# Revit family: 30. Секция фильтрования, вод. наг. и фреон. охл. ANR T4
name_source: partatom
category: Оборудование
revit_build: Autodesk Revit 2016 (Build: 20161004_0715(x64)
units: mm (PartAtom-declared; Revit-internal decimal feet)

## family parameters
Всегда вертикально = Да
На основе рабочей плоскости = Нет
Общий = Нет
При загрузке вырезать с полостями = Нет
Размер круглого соединителя = Использовать диаметр
Тип детали = Нормальный
Точка расчета площади = Нет

## types (10) — shared parameters
h = 130 мм
Д = 1625 мм
Д1 = 1605 мм
Д2 = 535 мм
Д3 = 268 мм
Е = 85 мм
Единица измерения = шт.
Завод изготовитель = KORF
Ключевая пометка = Вентиляция
Материал = Сталь серая
Наименование и тех.хар-ка = Секция фильтрования EU4, водяного нагрева вместе с фреоновым охлаждением
Раздел = ОВ
Размер В = 85 мм
Синий = Синий
высота ножек = 120 мм

## per-type parameters (varying)
| type | d | А | А1 | Б | Б1 | Вн | Высота | Г | Гн | Ж | З | И | Середина | Ширина |
| ANR 6 T4 | 32 мм | 1100 мм | 1080 мм | 1100 мм | 1080 мм | 735 мм | 1025 мм | 530 мм | 85 мм | 45 мм | 45 мм | 135 мм | 670 мм | 1025 мм |
| ANR 7 T4 | 38 мм | 1100 мм | 1080 мм | 1320 мм | 1300 мм | 985 мм | 1245 мм | 790 мм | 85 мм | 45 мм | 45 мм | 115 мм | 780 мм | 1025 мм |
| ANR 8 T4 | 38 мм | 1320 мм | 1300 мм | 1320 мм | 1300 мм | 985 мм | 1245 мм | 790 мм | 85 мм | 45 мм | 45 мм | 115 мм | 780 мм | 1245 мм |
| ANR 20 T4 | 51 мм | 1660 мм | 1640 мм | 1660 мм | 1640 мм | 1355 мм | 1585 мм | 1130 мм | 85 мм | 45 мм | 58 мм | 115 мм | 950 мм | 1585 мм |
| ANR 25 T4 | 64 мм | 2045 мм | 2025 мм | 2045 мм | 2025 мм | 1740 мм | 1970 мм | 1515 мм | 85 мм | 45 мм | 68 мм | 115 мм | 1143 мм | 1970 мм |
| ANR 30 T4 | 64 мм | 2485 мм | 2465 мм | 2045 мм | 2025 мм | 1685 мм | 1970 мм | 1515 мм | 100 мм | 70 мм | 30 мм | 115 мм | 1143 мм | 2410 мм |
| ANR 35 T4 | 76 мм | 2485 мм | 2465 мм | 2485 мм | 2465 мм | 2125 мм | 2410 мм | 1955 мм | 125 мм | 80 мм | 35 мм | 115 мм | 1363 мм | 2410 мм |
| ANR 40 T4 | 102 мм | 3320 мм | 3300 мм | 3320 мм | 3300 мм | 1355 мм | 3245 мм | 1130 мм | 100 мм | 70 мм | 30 мм | 115 мм | 1780 мм | 3245 мм |
| ANR 45 T4 | 80 мм | 3320 мм | 3300 мм | 4090 мм | 4070 мм | 1740 мм | 4015 мм | 1515 мм | 125 мм | 80 мм | 35 мм | 115 мм | 2165 мм | 3245 мм |
| ANR 12 T4 | 51 мм | 1435 мм | 1415 мм | 1435 мм | 1415 мм | 1060 мм | 1360 мм | 905 мм | 85 мм | 45 мм | 45 мм | 115 мм | 838 мм | 1360 мм |

note: column(s) folded — value = type name in every type: Тип, марка, обозначение
